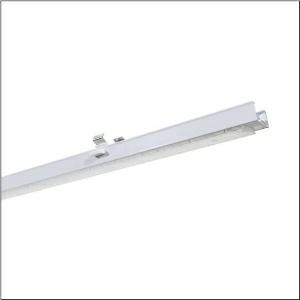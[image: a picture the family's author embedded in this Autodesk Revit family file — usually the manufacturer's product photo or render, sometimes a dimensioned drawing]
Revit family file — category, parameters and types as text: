
# Revit family: sanierungs-leuchteneinsatz_31_gen_2_51re12ma46b_1920
name_source: partatom
category: Lighting Fixtures
units: mm (PartAtom-declared; Revit-internal decimal feet)

## family parameters
Cut with Voids When Loaded = No
Host = Face
Light Source = No
Part Type = Normal
Room Calculation Point = No
Round Connector Dimension = Use Diameter
Shared = No

## types (1)
- --- (1 x LED, 6400 lm, 40 W, 4000K)
    Apparent Load = 40 VA
    CIE Flux Codes = 65 91 98 99 100
    Color Rendering = 80
    Color Temperature = 4000K
    Default Elevation = 1800 mm
    Description = Refurbishment luminaire insert Gen.2, luminaire insert, of extruded aluminium section, coated, traffic white (RAL 9016), length: 1.172mm, width: 91mm, height: 53mm, LED rated luminous flux: 6.400lm, light colour: 840, control gear: ON/OFF Multilumen, control gear: ECG Multilumen, with system connector: socket, mains connection: 220..240V, AC/DC, 0/50..60Hz, luminous flux adjustable on luminaire in four steps (3420/4540/5580/6630lm), connected load according to luminous flux setting (20/26/33/40W), primary light control with lens, of plastic, primary optical cover: cover, of PMMA, light emission: direct distribution, protection rating (complete): IP20, insulation class (complete): insulation class I (protective earthing), certification: CE, UKCA, permissible ambient temperature for indoor applications: -20..+40°C, packaging unit: 1 piece
    Height = 58 mm
    Lamp = 1 x LED
    Lamp Light Flux = 6400 lm
    Lamp Power = 40 W
    Lamp count = 1
    Length = 1172 mm
    Luminous efficacy = 160 lm/W
    Manufacturer = Siteco
    ModVariant = No
    Model = 51RE12MA46B
    Mounting Place = Ceiling
    Mounting Type = Pendant
    Number of Poles = 1
    OnlyDefault = Yes
    Power Factor = 1
    Product Name = Sanierungs-Leuchteneinsatz 31 Gen.2
    Product group = luminaire insert
    ProductGroupID = 902
    Protection Class = Protection class I
    Protection Degree = IP 20
    RLX_Detail_Level = 1
    RlxData = <blob elided: 19933 chars, md5=dea679a1>
    Socket = socket
    Standby Power = 0 W
    System Light Flux = 6400 lm
    System Power = 40 W
    Type Comments = factory setting: luminous flux: 100 % | (ON | ON) | 300 mA
    Type Image = l_1266702.jpg
    URL = http://relux.com
    VarID = @adj_090941
    Voltage = 0 V
    Weight = 0.00 kg
    Width = 65 mm

## geometry (parser evidence)
native form markers: Blend x4, Sweep x12
no freeform markers — native parametric forms only
